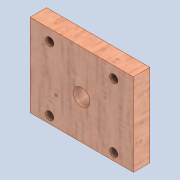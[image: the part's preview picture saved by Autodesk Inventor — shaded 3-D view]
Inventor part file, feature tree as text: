
AUTODESK INVENTOR PART (.ipt)
format: ipt  version: 2020 (Build 240168000, 168)  size: 263,680 bytes
history: native  units: mm
features: reference x4, other x3, extrude x2, sketch x2
ambient origin geometry x8: Origin, YZ Plane, XZ Plane, XY Plane, X Axis, Y Axis, Z Axis, Center Point
bodies: Solid1 (feature_tree)
feature tree (11):
  extrude  "Extrusion1"  Depth=40.0mm
  extrude  "Extrusion5"  Depth=8.0mm
  sketch  "Sketch1"  dims[d0=50.0mm d1=40.0mm]
  sketch  "Sketch5"  dims[d2=8.0mm d3=0.0mm d29=8.0mm d30=0.0mm d31=0.0mm d32=4.0mm d33=4.0mm d34=4.0mm d35=4.0mm]
  reference  "Reference1"
  reference  "Reference2"
  reference  "Reference3"
  reference  "Reference4"
  parser-record x1  (decoder bookkeeping rows leaked as tree rows — omitted from the tree; the rows remain in map.json)
  other  "0005-00-00 Ansamblu_General.iam"
  other  "0005-10-1001 NEMA17 - Motor de passo:4"
note: 1 file-system path scrubbed to <path> (originals preserved in map.json)
